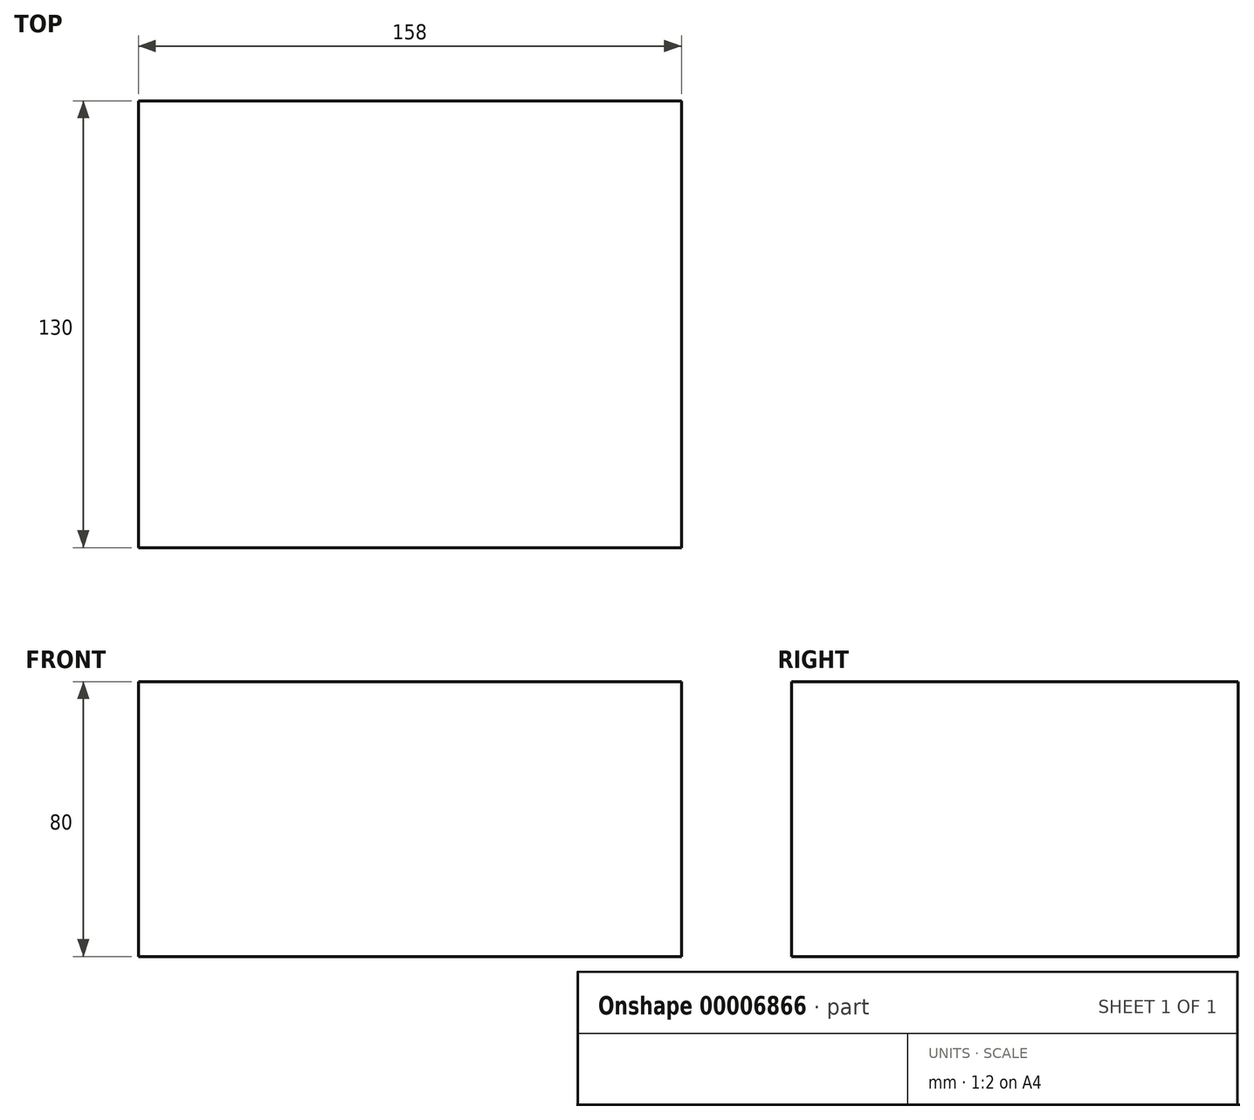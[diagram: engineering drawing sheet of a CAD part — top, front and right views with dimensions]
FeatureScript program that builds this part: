
annotation { "Feature Type Name" : "Feature", "Feature Type Description" : "" }
export const myFeature = defineFeature(function(context is Context, id is Id, definition is map)
    precondition{}
    {
        {
            var Q0;
            Q0=qCreatedBy(makeId("Top.planeOp"),FACE);
            var sketch = newSketch(context, id + "F0", { "sketchPlane" : qUnion([Q0])});
            skLineSegment(sketch, "E0.bottom", {"start": v(-77.03, 0) * mm, "end": v(80.97, 0) * mm});
            skLineSegment(sketch, "E0.top", {"start": v(-77.03, 130) * mm, "end": v(80.97, 130) * mm});
            skLineSegment(sketch, "E0.left", {"start": v(-77.03, 0) * mm, "end": v(-77.03, 130) * mm});
            skLineSegment(sketch, "E0.right", {"start": v(80.97, 0) * mm, "end": v(80.97, 130) * mm});
            skSolve(sketch);
        }
        {
            var Q0;
            Q0 = qSketchRegion(id + "F0", true);
            extrude(context, id + "F1", {"entities" : qUnion([Q0]), "depth" : 80 * mm});
        }
    });
